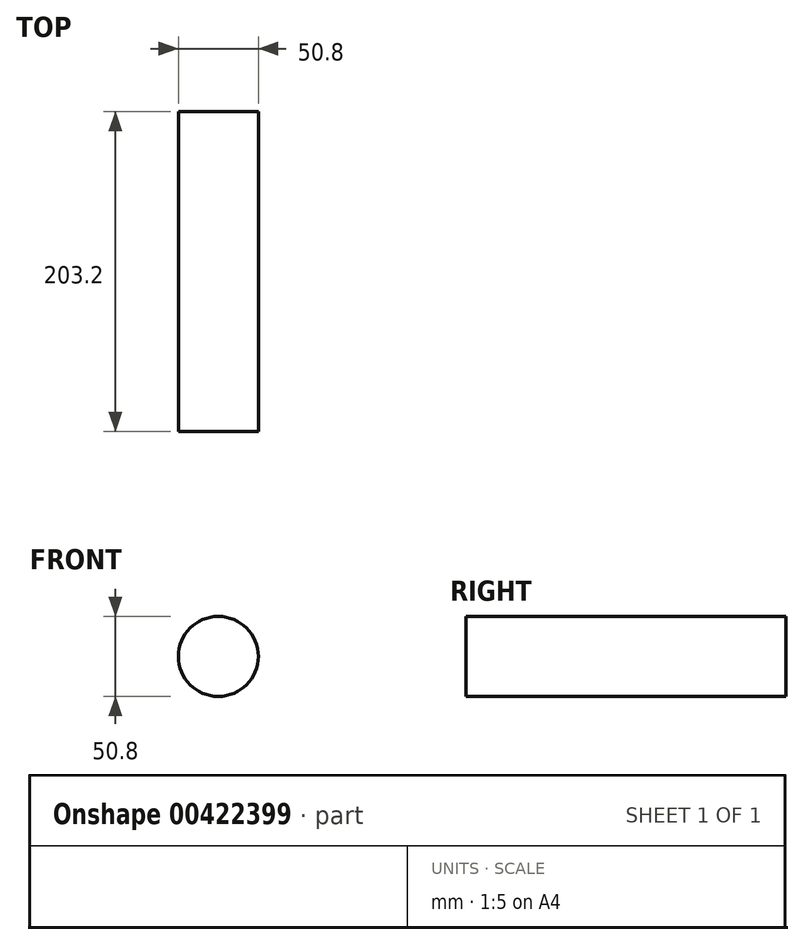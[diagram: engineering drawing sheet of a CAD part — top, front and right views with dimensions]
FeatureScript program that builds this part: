
annotation { "Feature Type Name" : "Feature", "Feature Type Description" : "" }
export const myFeature = defineFeature(function(context is Context, id is Id, definition is map)
    precondition{}
    {
        {
            var Q0;
            Q0=qCreatedBy(makeId("Front.planeOp"),FACE);
            var sketch = newSketch(context, id + "F0", { "sketchPlane" : qUnion([Q0])});
            skCircle(sketch, "E0", {"center": v(0, 0) * mm, "radius": 25.4 * mm});
            skSolve(sketch);
        }
        {
            var Q0;
            Q0=makeQuery(id+"F0.imprint","IMPRINT",FACE,{"disambiguationData":[TD([[makeQuery(id+"F0.imprint","IMPRINT",EDGE,{"derivedFrom":sQuery(id+"F0.wireOp",EDGE,"E0")}),1.0]])]});
            extrude(context, id + "F1", {"entities" : qUnion([Q0]), "depth" : 203.2 * mm});
        }
    });
